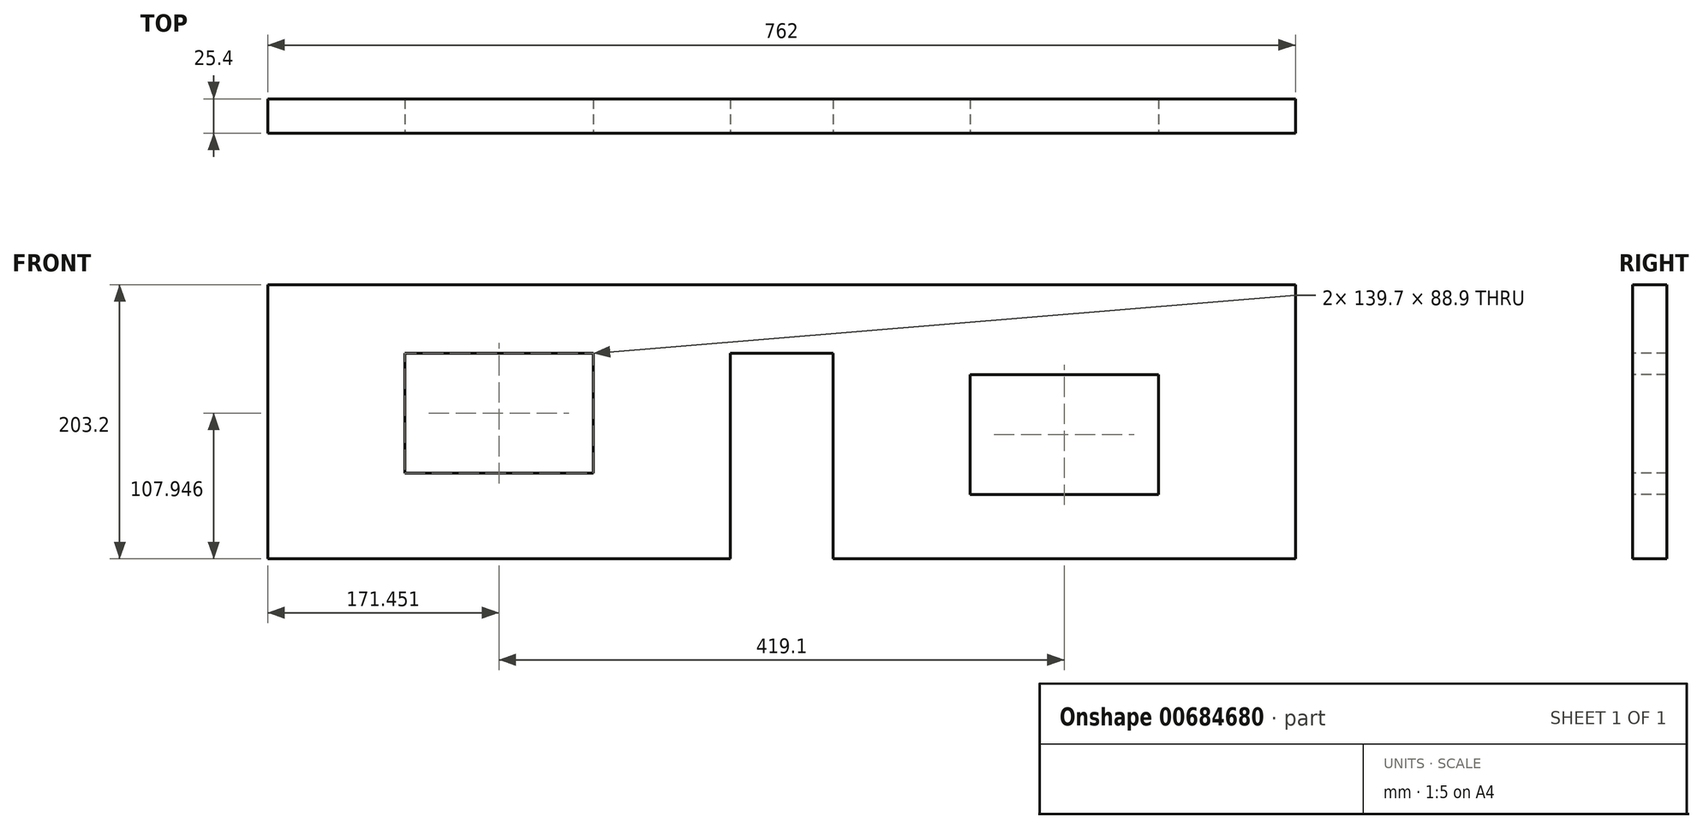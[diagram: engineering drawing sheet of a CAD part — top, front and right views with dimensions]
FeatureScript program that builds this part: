
annotation { "Feature Type Name" : "Feature", "Feature Type Description" : "" }
export const myFeature = defineFeature(function(context is Context, id is Id, definition is map)
    precondition{}
    {
        {
            var Q0;
            Q0=qCreatedBy(makeId("Front.planeOp"),FACE);
            var sketch = newSketch(context, id + "F0", { "sketchPlane" : qUnion([Q0])});
            skLineSegment(sketch, "E0.bottom", {"start": v(-382.35, -187.81) * mm, "end": v(379.65, -187.81) * mm});
            skLineSegment(sketch, "E0.top", {"start": v(-382.35, 15.39) * mm, "end": v(379.65, 15.39) * mm});
            skLineSegment(sketch, "E0.left", {"start": v(-382.35, -187.81) * mm, "end": v(-382.35, 15.39) * mm});
            skLineSegment(sketch, "E0.right", {"start": v(379.65, -187.81) * mm, "end": v(379.65, 15.39) * mm});
            skSolve(sketch);
        }
        {
            var Q0;
            Q0=qSketchRegion(id+"F0",true);
            extrude(context, id + "F1", {"entities" : qUnion([Q0]), "depth" : 25.4 * mm, "offsetDistance" : 25.4 * mm});
        }
        {
            var Q0;
            Q0=makeQuery(id+"F1.opExtrude","CAP_FACE",FACE,{"disambiguationData":[OSD([sQuery(id+"F0.wireOp",EDGE,"E0.bottom"),sQuery(id+"F0.wireOp",EDGE,"E0.top"),sQuery(id+"F0.wireOp",EDGE,"E0.left"),sQuery(id+"F0.wireOp",EDGE,"E0.right")])],"isStart":false});
            var sketch = newSketch(context, id + "F2", { "sketchPlane" : qUnion([Q0])});
            skLineSegment(sketch, "E1.bottom", {"start": v(-39.45, -187.81) * mm, "end": v(36.75, -187.81) * mm});
            skLineSegment(sketch, "E1.top", {"start": v(-39.45, -35.41) * mm, "end": v(36.75, -35.41) * mm});
            skLineSegment(sketch, "E1.left", {"start": v(-39.45, -187.81) * mm, "end": v(-39.45, -35.41) * mm});
            skLineSegment(sketch, "E1.right", {"start": v(36.75, -187.81) * mm, "end": v(36.75, -35.41) * mm});
            skLineSegment(sketch, "E2.bottom", {"start": v(-280.75, -124.31) * mm, "end": v(-141.05, -124.31) * mm});
            skLineSegment(sketch, "E2.top", {"start": v(-280.75, -35.41) * mm, "end": v(-141.05, -35.41) * mm});
            skLineSegment(sketch, "E2.left", {"start": v(-280.75, -124.31) * mm, "end": v(-280.75, -35.41) * mm});
            skLineSegment(sketch, "E2.right", {"start": v(-141.05, -124.31) * mm, "end": v(-141.05, -35.41) * mm});
            skLineSegment(sketch, "E3.bottom", {"start": v(138.35, -51.44) * mm, "end": v(278.05, -51.44) * mm});
            skLineSegment(sketch, "E3.top", {"start": v(138.35, -140.34) * mm, "end": v(278.05, -140.34) * mm});
            skLineSegment(sketch, "E3.left", {"start": v(138.35, -51.44) * mm, "end": v(138.35, -140.34) * mm});
            skLineSegment(sketch, "E3.right", {"start": v(278.05, -51.44) * mm, "end": v(278.05, -140.34) * mm});
            skSolve(sketch);
        }
        {
            var Q0;
            Q0=makeQuery(id+"F2.imprint","IMPRINT",FACE,{"disambiguationData":[TD([[makeQuery(id+"F2.imprint","IMPRINT",EDGE,{"derivedFrom":sQuery(id+"F2.wireOp",EDGE,"E2.bottom")}),1.0]])]});
            extrude(context, id + "F3", {"entities" : qUnion([Q0]), "operationType" : NewBodyOperationType.REMOVE, "oppositeDirection" : true, "depth" : 50.8 * mm, "offsetDistance" : 25.4 * mm});
        }
        {
            var Q0;
            Q0=makeQuery(id+"F2.imprint","IMPRINT",FACE,{"disambiguationData":[TD([[makeQuery(id+"F2.imprint","IMPRINT",EDGE,{"derivedFrom":sQuery(id+"F2.wireOp",EDGE,"E1.bottom")}),1.0]])]});
            extrude(context, id + "F4", {"entities" : qUnion([Q0]), "operationType" : NewBodyOperationType.REMOVE, "oppositeDirection" : true, "depth" : 50.8 * mm, "offsetDistance" : 25.4 * mm});
        }
        {
            var Q0;
            Q0=makeQuery(id+"F2.imprint","IMPRINT",FACE,{"disambiguationData":[TD([[makeQuery(id+"F2.imprint","IMPRINT",EDGE,{"derivedFrom":sQuery(id+"F2.wireOp",EDGE,"E3.bottom")}),-1.0]])]});
            extrude(context, id + "F5", {"entities" : qUnion([Q0]), "operationType" : NewBodyOperationType.REMOVE, "oppositeDirection" : true, "depth" : 50.8 * mm, "offsetDistance" : 25.4 * mm});
        }
    });
